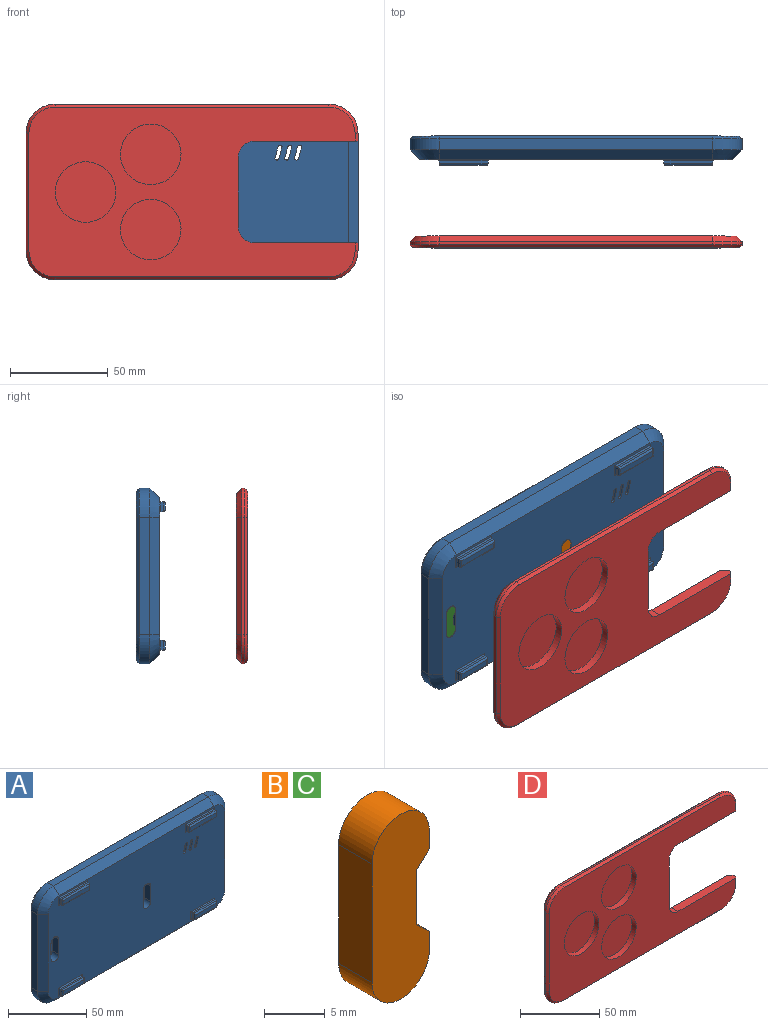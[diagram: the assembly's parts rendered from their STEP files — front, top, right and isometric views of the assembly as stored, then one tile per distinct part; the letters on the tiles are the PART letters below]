
ASSEMBLY  parts=4 mates=3
PART A: 131 faces, bbox 170.2x15.2x90.2 mm
  f0: plane 92.83x73.17mm, normal (0,1,0), area 3427.2mm2, adj f2,f44,f45,f46,f47,f48,f49,f50
  f1: plane 160x80mm, normal (0,-1,0), area 11812.8mm2, adj f26,f27,f28,f29,f30,f31,f32,f33
  f2: extruded ~36.49x27.03mm, area 597.8mm2, adj f0,f19,f45,f50,f95,f96,f97
  f3: plane 12x6mm, normal (1,0,0), area 72mm2, adj f4,f10,f19,f43
  f4: cylinder r=2mm len=6mm, axis (0,1,0), area 37.7mm2, adj f3,f5,f19,f43
  f5: plane 12x6mm, normal (-1,0,0), area 72mm2, adj f4,f10,f19,f43
  f6: cylinder r=2mm len=6mm, axis (0,1,0), area 37.7mm2, adj f7,f9,f19,f38
  f7: plane 12x6mm, normal (-1,0,0), area 72mm2, adj f6,f8,f19,f38
  f8: cylinder r=2mm len=6mm, axis (0,1,0), area 37.7mm2, adj f7,f9,f19,f38
  f9: plane 12x6mm, normal (1,0,0), area 72mm2, adj f6,f8,f19,f38
  f10: cylinder r=2mm len=6mm, axis (0,1,0), area 37.7mm2, adj f3,f5,f19,f43
  f11: plane 60x5.5mm, normal (1,0,0), area 330mm2, adj f12,f18,f32,f93
  f12: cylinder r=15mm len=15mm, axis (0,1,0), area 129.6mm2, adj f11,f13,f30,f91
  f13: plane 140x5.5mm, normal (0,0,1), area 770mm2, adj f12,f14,f28,f89
  f14: cylinder r=15mm len=15mm, axis (0,1,0), area 129.6mm2, adj f13,f15,f26,f87
  f15: plane 60x5.5mm, normal (-1,0,0), area 330mm2, adj f14,f16,f27,f88
  f16: cylinder r=15mm len=15mm, axis (0,1,0), area 129.6mm2, adj f15,f17,f29,f90
  f17: plane 140x5.5mm, normal (0,0,-1), area 770mm2, adj f16,f18,f31,f92
  f18: cylinder r=15mm len=15mm, axis (0,1,0), area 129.6mm2, adj f11,f17,f33,f94
  f19: plane 167x87mm, normal (0,1,0), area 8279.9mm2, adj f2,f3,f4,f5,f6,f7,f8,f9
  f20: cylinder r=15.5mm len=31mm, axis (0,1,0), area 584.3mm2, adj f19,f21
  f21: plane 31x31mm, normal (0,1,0), area 754.8mm2, adj f20
  f22: cylinder r=15.5mm len=31mm, axis (0,1,0), area 584.3mm2, adj f19,f23
  f23: plane 31x31mm, normal (0,1,0), area 754.8mm2, adj f22
  f24: cylinder r=15.5mm len=31mm, axis (0,1,0), area 584.3mm2, adj f19,f25
  f25: plane 31x31mm, normal (0,1,0), area 754.8mm2, adj f24
  f26: cone r=10mm half-angle=45deg, axis (0,1,0), area 138.8mm2, adj f1,f14,f27,f28
  f27: plane 60x5mm, normal (-0.71,-0.71,0), area 424.3mm2, adj f1,f15,f26,f29
  f28: plane 140x5mm, normal (0,-0.71,0.71), area 989.9mm2, adj f1,f13,f26,f30
  f29: cone r=10mm half-angle=45deg, axis (0,1,0), area 138.8mm2, adj f1,f16,f27,f31
  f30: cone r=10mm half-angle=45deg, axis (0,1,0), area 138.8mm2, adj f1,f12,f28,f32
  f31: plane 140x5mm, normal (0,-0.71,-0.71), area 989.9mm2, adj f1,f17,f29,f33
  f32: plane 60x5mm, normal (0.71,-0.71,0), area 424.3mm2, adj f1,f11,f30,f33
  f33: cone r=10mm half-angle=45deg, axis (0,1,0), area 138.8mm2, adj f1,f18,f31,f32
  f34: plane 12x6mm, normal (1,0,0), area 72mm2, adj f1,f35,f37,f38
  f35: cylinder r=3.5mm len=7mm, axis (0,-1,0), area 66mm2, adj f1,f34,f36,f38
  f36: plane 12x6mm, normal (-1,0,0), area 72mm2, adj f1,f35,f37,f38
  f37: cylinder r=3.5mm len=7mm, axis (0,-1,0), area 66mm2, adj f1,f34,f36,f38
  f38: plane 19x7mm, normal (0,-1,0), area 61.9mm2, adj f6,f7,f8,f9,f34,f35,f36,f37
  f39: cylinder r=3.5mm len=7mm, axis (0,-1,0), area 66mm2, adj f1,f40,f42,f43
  f40: plane 12x6mm, normal (1,0,0), area 72mm2, adj f1,f39,f41,f43
  f41: cylinder r=3.5mm len=7mm, axis (0,-1,0), area 66mm2, adj f1,f40,f42,f43
  f42: plane 12x6mm, normal (-1,0,0), area 72mm2, adj f1,f39,f41,f43
  f43: plane 19x7mm, normal (0,-1,0), area 61.9mm2, adj f3,f4,f5,f10,f39,f40,f41,f42
  f44: cylinder r=31.5mm len=63mm, axis (0,1,0), area 1985.3mm2, adj f0,f19,f48,f49
  f45: cylinder r=3.16mm len=10.8mm, axis (0,1,0), area 111.2mm2, adj f0,f2,f19,f46,f95
  f46: extruded ~35.51x21.45mm, area 548.1mm2, adj f0,f19,f45,f47
  f47: plane 10.8x2.15mm, normal (0.71,0,0.71), area 32.9mm2, adj f0,f19,f46,f48
  f48: plane 12.03x12.03mm, normal (0.71,0,-0.71), area 183.8mm2, adj f0,f19,f44,f47
  f49: plane 12.03x12.03mm, normal (-0.71,0,0.71), area 183.8mm2, adj f0,f19,f44,f50
  f50: plane 10.8x2.15mm, normal (0.71,0,0.71), area 32.9mm2, adj f0,f2,f19,f49
  f51: plane 25x1.3mm, normal (0,0,1), area 32.5mm2, adj f52,f54,f84,f111
  f52: plane 5x1.3mm, normal (-1,0,0), area 6.5mm2, adj f51,f53,f86,f113
  f53: plane 25x1.3mm, normal (0,0,-1), area 32.5mm2, adj f52,f54,f85,f112
  f54: plane 5x1.3mm, normal (1,0,0), area 6.5mm2, adj f51,f53,f83,f110
  f55: plane 23x3mm, normal (0,-1,0), area 69mm2, adj f83,f84,f85,f86
  f56: plane 5x1.3mm, normal (-1,0,0), area 6.5mm2, adj f57,f59,f79,f106
  f57: plane 20x1.3mm, normal (0,0,-1), area 26mm2, adj f56,f58,f81,f108
  f58: plane 5x1.3mm, normal (1,0,0), area 6.5mm2, adj f57,f59,f82,f109
  f59: plane 20x1.3mm, normal (0,0,1), area 26mm2, adj f56,f58,f80,f107
  f60: plane 18x3mm, normal (0,-1,0), area 54mm2, adj f79,f80,f81,f82
  f61: plane 5x1.3mm, normal (1,0,0), area 6.5mm2, adj f62,f64,f76,f103
  f62: plane 25x1.3mm, normal (0,0,1), area 32.5mm2, adj f61,f63,f78,f105
  f63: plane 5x1.3mm, normal (-1,0,0), area 6.5mm2, adj f62,f64,f77,f104
  f64: plane 25x1.3mm, normal (0,0,-1), area 32.5mm2, adj f61,f63,f75,f102
  f65: plane 23x3mm, normal (0,-1,0), area 69mm2, adj f75,f76,f77,f78
  f66: plane 5x1.3mm, normal (1,0,0), area 6.5mm2, adj f67,f69,f72,f99
  f67: plane 20x1.3mm, normal (0,0,1), area 26mm2, adj f66,f68,f74,f101
  f68: plane 5x1.3mm, normal (-1,0,0), area 6.5mm2, adj f67,f69,f73,f100
  f69: plane 20x1.3mm, normal (0,0,-1), area 26mm2, adj f66,f68,f71,f98
  f70: plane 18x3mm, normal (0,-1,0), area 54mm2, adj f71,f72,f73,f74
  f71: cylinder r=1mm len=20mm, axis (-1,0,0), area 29.8mm2, adj f69,f70,f72,f73
  f72: cylinder r=1mm len=5mm, axis (0,0,-1), area 6.3mm2, adj f66,f70,f71,f74
  f73: cylinder r=1mm len=5mm, axis (0,0,1), area 6.3mm2, adj f68,f70,f71,f74
  f74: cylinder r=1mm len=20mm, axis (1,0,0), area 29.8mm2, adj f67,f70,f72,f73
  f75: cylinder r=1mm len=25mm, axis (-1,0,0), area 37.7mm2, adj f64,f65,f76,f77
  f76: cylinder r=1mm len=5mm, axis (0,0,-1), area 6.3mm2, adj f61,f65,f75,f78
  f77: cylinder r=1mm len=5mm, axis (0,0,1), area 6.3mm2, adj f63,f65,f75,f78
  f78: cylinder r=1mm len=25mm, axis (1,0,0), area 37.7mm2, adj f62,f65,f76,f77
  f79: cylinder r=1mm len=5mm, axis (0,0,1), area 6.3mm2, adj f56,f60,f80,f81
  f80: cylinder r=1mm len=20mm, axis (1,0,0), area 29.8mm2, adj f59,f60,f79,f82
  f81: cylinder r=1mm len=20mm, axis (-1,0,0), area 29.8mm2, adj f57,f60,f79,f82
  f82: cylinder r=1mm len=5mm, axis (0,0,-1), area 6.3mm2, adj f58,f60,f80,f81
  f83: cylinder r=1mm len=5mm, axis (0,0,-1), area 6.3mm2, adj f54,f55,f84,f85
  f84: cylinder r=1mm len=25mm, axis (1,0,0), area 37.7mm2, adj f51,f55,f83,f86
  f85: cylinder r=1mm len=25mm, axis (-1,0,0), area 37.7mm2, adj f53,f55,f83,f86
  f86: cylinder r=1mm len=5mm, axis (0,0,1), area 6.3mm2, adj f52,f55,f84,f85
  f87: cone r=15mm half-angle=45deg, axis (0,-1,0), area 47.5mm2, adj f14,f19,f88,f89
  f88: plane 60x1.5mm, normal (-0.71,0.71,0), area 127.3mm2, adj f15,f19,f87,f90
  f89: plane 140x1.5mm, normal (0,0.71,0.71), area 297mm2, adj f13,f19,f87,f91
  f90: cone r=15mm half-angle=45deg, axis (0,-1,0), area 47.5mm2, adj f16,f19,f88,f92
  f91: cone r=15mm half-angle=45deg, axis (0,-1,0), area 47.5mm2, adj f12,f19,f89,f93
  f92: plane 140x1.5mm, normal (0,0.71,-0.71), area 297mm2, adj f17,f19,f90,f94
  f93: plane 60x1.5mm, normal (0.71,0.71,0), area 127.3mm2, adj f11,f19,f91,f94
  f94: cone r=15mm half-angle=45deg, axis (0,-1,0), area 47.5mm2, adj f18,f19,f92,f93
  f95: extruded ~8.16x7.16mm, area 21.7mm2, adj f2,f19,f45,f97
  f96: plane 5.88x4.68mm, normal (0,-1,0), area 6.4mm2, adj f2,f97
  f97: bspline ~8.17x7.16mm, area 16.4mm2, adj f2,f95,f96
  f98: cylinder r=0.7mm len=21.4mm, axis (1,0,0), area 22.8mm2, adj f1,f69,f99,f100
  f99: cylinder r=0.7mm len=6.4mm, axis (0,0,1), area 6.3mm2, adj f1,f66,f98,f101
  f100: cylinder r=0.7mm len=6.4mm, axis (0,0,-1), area 6.3mm2, adj f1,f68,f98,f101
  f101: cylinder r=0.7mm len=21.4mm, axis (-1,0,0), area 22.8mm2, adj f1,f67,f99,f100
  f102: cylinder r=0.7mm len=26.4mm, axis (1,0,0), area 28.3mm2, adj f1,f64,f103,f104
  f103: cylinder r=0.7mm len=6.4mm, axis (0,0,1), area 6.3mm2, adj f1,f61,f102,f105
  f104: cylinder r=0.7mm len=6.4mm, axis (0,0,-1), area 6.3mm2, adj f1,f63,f102,f105
  f105: cylinder r=0.7mm len=26.4mm, axis (-1,0,0), area 28.3mm2, adj f1,f62,f103,f104
  f106: cylinder r=0.7mm len=6.4mm, axis (0,0,-1), area 6.3mm2, adj f1,f56,f107,f108
  f107: cylinder r=0.7mm len=21.4mm, axis (-1,0,0), area 22.8mm2, adj f1,f59,f106,f109
  f108: cylinder r=0.7mm len=21.4mm, axis (1,0,0), area 22.8mm2, adj f1,f57,f106,f109
  f109: cylinder r=0.7mm len=6.4mm, axis (0,0,1), area 6.3mm2, adj f1,f58,f107,f108
  f110: cylinder r=0.7mm len=6.4mm, axis (0,0,1), area 6.3mm2, adj f1,f54,f111,f112
  f111: cylinder r=0.7mm len=26.4mm, axis (-1,0,0), area 28.3mm2, adj f1,f51,f110,f113
  f112: cylinder r=0.7mm len=26.4mm, axis (1,0,0), area 28.3mm2, adj f1,f53,f110,f113
  f113: cylinder r=0.7mm len=6.4mm, axis (0,0,-1), area 6.3mm2, adj f1,f52,f111,f112
  f114: plane 55.8x55.8mm, normal (0,1,0), area 253.5mm2, adj f115,f116,f117,f118
  f115: cylinder r=27.9mm len=55.8mm, axis (0,-1,0), area 591.6mm2, adj f0,f114,f117,f118
  f116: cylinder r=25.9mm len=51.8mm, axis (0,-1,0), area 549.2mm2, adj f0,f114,f117,f118
  f117: plane 4.5x2mm, normal (0,0,-1), area 9mm2, adj f0,f114,f115,f116
  f118: plane 4.5x2mm, normal (-1,0,0), area 9mm2, adj f0,f114,f115,f116
  f119: cylinder r=1.07mm len=2.07mm, axis (0,-1,0), area 3.4mm2, adj f0,f1,f120,f122
  f120: plane 6x1.61mm, normal (0.97,0,-0.26), area 7.5mm2, adj f0,f1,f119,f121
  f121: cylinder r=1.07mm len=2.07mm, axis (0,-1,0), area 3.4mm2, adj f0,f1,f120,f122
  f122: plane 6x1.61mm, normal (-0.97,0,0.26), area 7.5mm2, adj f0,f1,f119,f121
  f123: cylinder r=1.07mm len=2.07mm, axis (0,-1,0), area 3.4mm2, adj f0,f1,f124,f126
  f124: plane 6x1.61mm, normal (0.97,0,-0.26), area 7.5mm2, adj f0,f1,f123,f125
  f125: cylinder r=1.07mm len=2.07mm, axis (0,-1,0), area 3.4mm2, adj f0,f1,f124,f126
  f126: plane 6x1.61mm, normal (-0.97,0,0.26), area 7.5mm2, adj f0,f1,f123,f125
  f127: cylinder r=1.07mm len=2.07mm, axis (0,-1,0), area 3.4mm2, adj f0,f1,f128,f130
  f128: plane 6x1.61mm, normal (0.97,0,-0.26), area 7.5mm2, adj f0,f1,f127,f129
  f129: cylinder r=1.07mm len=2.07mm, axis (0,-1,0), area 3.4mm2, adj f0,f1,f128,f130
  f130: plane 6x1.61mm, normal (-0.97,0,0.26), area 7.5mm2, adj f0,f1,f127,f129
PART B: 11 faces, bbox 6.7x3.9x18.7 mm
  f0: plane 3.9x1.83mm, normal (1,0,0), area 7.1mm2, adj f3,f5,f6,f8
  f1: cylinder r=3.35mm len=6.7mm, axis (0,-1,0), area 41mm2, adj f2,f4,f5,f6
  f2: plane 12x3.9mm, normal (-1,0,0), area 46.8mm2, adj f1,f3,f5,f6
  f3: cylinder r=3.35mm len=6.7mm, axis (0,-1,0), area 41mm2, adj f0,f2,f5,f6
  f4: plane 3.9x1.83mm, normal (1,0,0), area 7.1mm2, adj f1,f5,f6,f7
  f5: plane 18.7x6.7mm, normal (0,1,0), area 97.3mm2, adj f0,f1,f2,f3,f4,f7,f8,f10
  f6: plane 18.7x6.7mm, normal (0,-1,0), area 105.4mm2, adj f0,f1,f2,f3,f4,f7,f8,f9
  f7: plane 3.97x3.9mm, normal (0.68,0,-0.73), area 12.2mm2, adj f4,f5,f6,f9,f10
  f8: plane 3.97x3.9mm, normal (0.68,0,0.73), area 12.2mm2, adj f0,f5,f6,f9,f10
  f9: plane 5.57x1.4mm, normal (1,0,0), area 7.8mm2, adj f6,f7,f8,f10
  f10: plane 5.57x2.5mm, normal (0.71,0.71,0), area 11.4mm2, adj f5,f7,f8,f9
PART C: same geometry as B
PART D: 76 faces, bbox 170x6x90 mm
  f0: plane 164x84mm, normal (0,1,0), area 9859mm2, adj f1,f18,f19,f20,f21,f22,f23,f24
  f1: plane 4x3mm, normal (0.71,0.71,0), area 17mm2, adj f0,f10,f20,f26
  f2: plane 4x1.5mm, normal (1,0,0), area 6mm2, adj f9,f18,f28,f73
  f3: plane 167x87mm, normal (0,-1,0), area 9026.2mm2, adj f11,f12,f13,f26,f27,f28,f65,f66
  f4: plane 140x1.5mm, normal (0,0,1), area 210mm2, adj f5,f14,f22,f67
  f5: cylinder r=15mm len=15mm, axis (0,1,0), area 35.3mm2, adj f4,f6,f24,f68
  f6: plane 60x1.5mm, normal (-1,0,0), area 90mm2, adj f5,f7,f25,f69
  f7: cylinder r=15mm len=15mm, axis (0,1,0), area 35.3mm2, adj f6,f8,f23,f70
  f8: plane 140x1.5mm, normal (0,0,-1), area 210mm2, adj f7,f9,f21,f71
  f9: cylinder r=15mm len=15mm, axis (0,1,0), area 35.3mm2, adj f2,f8,f19,f72
  f10: plane 4x1.5mm, normal (1,0,0), area 6mm2, adj f1,f14,f26,f65
  f11: cylinder r=15.5mm len=31mm, axis (0,1,0), area 389.6mm2, adj f3,f15
  f12: cylinder r=15.5mm len=31mm, axis (0,1,0), area 389.6mm2, adj f3,f16
  f13: cylinder r=15.5mm len=31mm, axis (0,1,0), area 389.6mm2, adj f3,f17
  f14: cylinder r=15mm len=15mm, axis (0,1,0), area 35.3mm2, adj f4,f10,f20,f66
  f15: plane 31x31mm, normal (0,-1,0), area 754.8mm2, adj f11
  f16: plane 31x31mm, normal (0,-1,0), area 754.8mm2, adj f12
  f17: plane 31x31mm, normal (0,-1,0), area 754.8mm2, adj f13
  f18: plane 4x3mm, normal (0.71,0.71,0), area 17mm2, adj f0,f2,f19,f28
  f19: cone r=15mm half-angle=45deg, axis (0,-1,0), area 90mm2, adj f0,f9,f18,f21
  f20: cone r=15mm half-angle=45deg, axis (0,-1,0), area 90mm2, adj f0,f1,f14,f22
  f21: plane 140x3mm, normal (0,0.71,-0.71), area 594mm2, adj f0,f8,f19,f23
  f22: plane 140x3mm, normal (0,0.71,0.71), area 594mm2, adj f0,f4,f20,f24
  f23: cone r=15mm half-angle=45deg, axis (0,-1,0), area 90mm2, adj f0,f7,f21,f25
  f24: cone r=15mm half-angle=45deg, axis (0,-1,0), area 90mm2, adj f0,f5,f22,f25
  f25: plane 60x3mm, normal (-0.71,0.71,0), area 254.6mm2, adj f0,f6,f23,f24
  f26: plane 53.3x6mm, normal (0,0,-1), area 314.2mm2, adj f0,f1,f3,f10,f65,f74
  f27: plane 36x6mm, normal (1,0,0), area 216mm2, adj f0,f3,f74,f75
  f28: plane 53.3x6mm, normal (0,0,1), area 314.2mm2, adj f0,f2,f3,f18,f73,f75
  f29: plane 5.8x2.8mm, normal (1,0,0), area 16.2mm2, adj f30,f32,f33,f51
  f30: plane 25.8x2.8mm, normal (0,0,-1), area 72.2mm2, adj f29,f31,f33,f52
  f31: plane 5.8x2.8mm, normal (-1,0,0), area 16.2mm2, adj f30,f32,f33,f50
  f32: plane 25.8x2.8mm, normal (0,0,1), area 72.2mm2, adj f29,f31,f33,f49
  f33: plane 25.8x5.8mm, normal (0,1,0), area 149.6mm2, adj f29,f30,f31,f32
  f34: plane 20.8x2.8mm, normal (0,0,1), area 58.2mm2, adj f35,f37,f38,f56
  f35: plane 5.8x2.8mm, normal (1,0,0), area 16.2mm2, adj f34,f36,f38,f54
  f36: plane 20.8x2.8mm, normal (0,0,-1), area 58.2mm2, adj f35,f37,f38,f53
  f37: plane 5.8x2.8mm, normal (-1,0,0), area 16.2mm2, adj f34,f36,f38,f55
  f38: plane 20.8x5.8mm, normal (0,1,0), area 120.6mm2, adj f34,f35,f36,f37
  f39: plane 5.8x2.8mm, normal (-1,0,0), area 16.2mm2, adj f40,f42,f43,f58
  f40: plane 20.8x2.8mm, normal (0,0,1), area 58.2mm2, adj f39,f41,f43,f60
  f41: plane 5.8x2.8mm, normal (1,0,0), area 16.2mm2, adj f40,f42,f43,f59
  f42: plane 20.8x2.8mm, normal (0,0,-1), area 58.2mm2, adj f39,f41,f43,f57
  f43: plane 20.8x5.8mm, normal (0,1,0), area 120.6mm2, adj f39,f40,f41,f42
  f44: plane 5.8x2.8mm, normal (1,0,0), area 16.2mm2, adj f45,f47,f48,f62
  f45: plane 25.8x2.8mm, normal (0,0,-1), area 72.2mm2, adj f44,f46,f48,f64
  f46: plane 5.8x2.8mm, normal (-1,0,0), area 16.2mm2, adj f45,f47,f48,f63
  f47: plane 25.8x2.8mm, normal (0,0,1), area 72.2mm2, adj f44,f46,f48,f61
  f48: plane 25.8x5.8mm, normal (0,1,0), area 149.6mm2, adj f44,f45,f46,f47
  f49: plane 27.8x1mm, normal (0,0.71,0.71), area 37.9mm2, adj f0,f32,f50,f51
  f50: plane 7.8x1mm, normal (-0.71,0.71,0), area 9.6mm2, adj f0,f31,f49,f52
  f51: plane 7.8x1mm, normal (0.71,0.71,0), area 9.6mm2, adj f0,f29,f49,f52
  f52: plane 27.8x1mm, normal (0,0.71,-0.71), area 37.9mm2, adj f0,f30,f50,f51
  f53: plane 22.8x1mm, normal (0,0.71,-0.71), area 30.8mm2, adj f0,f36,f54,f55
  f54: plane 7.8x1mm, normal (0.71,0.71,0), area 9.6mm2, adj f0,f35,f53,f56
  f55: plane 7.8x1mm, normal (-0.71,0.71,0), area 9.6mm2, adj f0,f37,f53,f56
  f56: plane 22.8x1mm, normal (0,0.71,0.71), area 30.8mm2, adj f0,f34,f54,f55
  f57: plane 22.8x1mm, normal (0,0.71,-0.71), area 30.8mm2, adj f0,f42,f58,f59
  f58: plane 7.8x1mm, normal (-0.71,0.71,0), area 9.6mm2, adj f0,f39,f57,f60
  f59: plane 7.8x1mm, normal (0.71,0.71,0), area 9.6mm2, adj f0,f41,f57,f60
  f60: plane 22.8x1mm, normal (0,0.71,0.71), area 30.8mm2, adj f0,f40,f58,f59
  f61: plane 27.8x1mm, normal (0,0.71,0.71), area 37.9mm2, adj f0,f47,f62,f63
  f62: plane 7.8x1mm, normal (0.71,0.71,0), area 9.6mm2, adj f0,f44,f61,f64
  f63: plane 7.8x1mm, normal (-0.71,0.71,0), area 9.6mm2, adj f0,f46,f61,f64
  f64: plane 27.8x1mm, normal (0,0.71,-0.71), area 37.9mm2, adj f0,f45,f62,f63
  f65: plane 4x1.5mm, normal (0.71,-0.71,0), area 8.5mm2, adj f3,f10,f26,f66
  f66: cone r=13.5mm half-angle=45deg, axis (0,1,0), area 47.5mm2, adj f3,f14,f65,f67
  f67: plane 140x1.5mm, normal (0,-0.71,0.71), area 297mm2, adj f3,f4,f66,f68
  f68: cone r=13.5mm half-angle=45deg, axis (0,1,0), area 47.5mm2, adj f3,f5,f67,f69
  f69: plane 60x1.5mm, normal (-0.71,-0.71,0), area 127.3mm2, adj f3,f6,f68,f70
  f70: cone r=13.5mm half-angle=45deg, axis (0,1,0), area 47.5mm2, adj f3,f7,f69,f71
  f71: plane 140x1.5mm, normal (0,-0.71,-0.71), area 297mm2, adj f3,f8,f70,f72
  f72: cone r=13.5mm half-angle=45deg, axis (0,1,0), area 47.5mm2, adj f3,f9,f71,f73
  f73: plane 4x1.5mm, normal (0.71,-0.71,0), area 8.5mm2, adj f2,f3,f28,f72
  f74: cylinder r=8mm len=8mm, axis (0,1,0), area 75.4mm2, adj f0,f3,f26,f27
  f75: cylinder r=8mm len=8mm, axis (0,-1,0), area 75.4mm2, adj f0,f3,f27,f28
PLACE A t=(-72.25,-8.58,-2.67)mm fixed
PLACE B t=(11.25,-8.58,-2.67)mm
PLACE C t=(-72.25,-8.58,-2.67)mm
PLACE D t=(-72.25,-22.78,-2.67)mm
MATE fastened B.f1 <-> A.f6  axis (0,-1,0) through (-30.5,-20.58,3.33)mm
MATE slider D.f33 <-> A.f55  axis (0,1,0) through (-97.5,-63.58,32.83)mm
MATE fastened C.f1 <-> A.f4  axis (0,-1,0) through (-114,-20.58,3.33)mm
